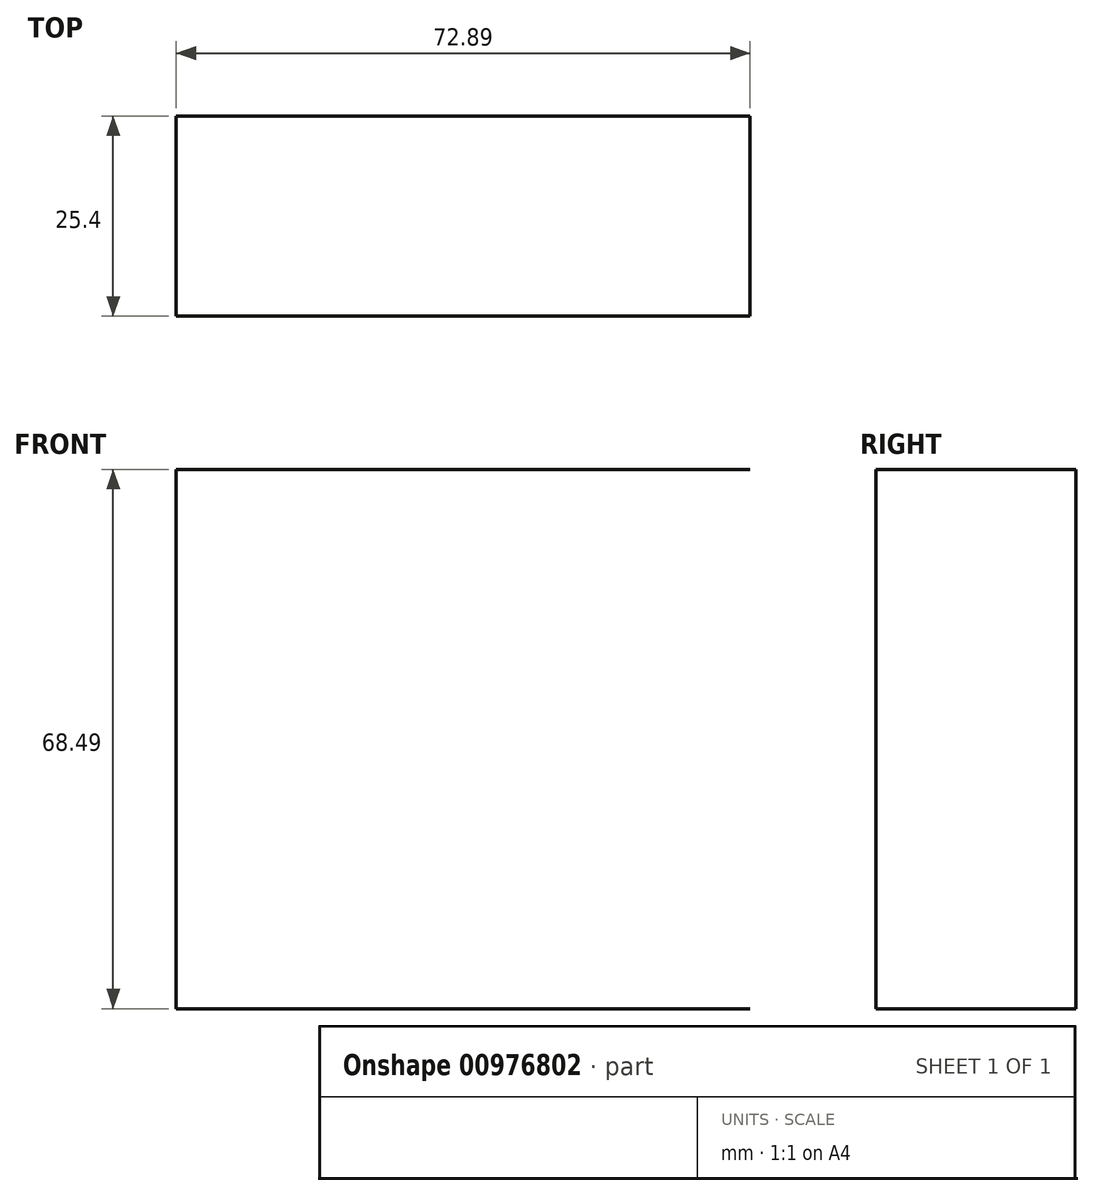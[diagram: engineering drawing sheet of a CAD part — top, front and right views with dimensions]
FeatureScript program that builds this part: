
annotation { "Feature Type Name" : "Feature", "Feature Type Description" : "" }
export const myFeature = defineFeature(function(context is Context, id is Id, definition is map)
    precondition{}
    {
        {
            var Q0;
            Q0=qCreatedBy(makeId("Front.planeOp"),FACE);
            var sketch = newSketch(context, id + "F0", { "sketchPlane" : qUnion([Q0])});
            skLineSegment(sketch, "E0.bottom", {"start": v(0, 0) * mm, "end": v(0, 0) * mm});
            skLineSegment(sketch, "E0.top", {"start": v(0, 0) * mm, "end": v(0, 0) * mm});
            skLineSegment(sketch, "E0.left", {"start": v(0, 0) * mm, "end": v(0, 0) * mm});
            skLineSegment(sketch, "E0.right", {"start": v(0, 0) * mm, "end": v(0, 0) * mm});
            skLineSegment(sketch, "E1.bottom", {"start": v(0, 0) * mm, "end": v(-72.89, 0) * mm});
            skLineSegment(sketch, "E1.top", {"start": v(0, -68.49) * mm, "end": v(-72.89, -68.49) * mm});
            skLineSegment(sketch, "E1.left", {"start": v(0, 0) * mm, "end": v(0, -68.49) * mm, "construction": true});
            skLineSegment(sketch, "E1.right", {"start": v(-72.89, 0) * mm, "end": v(-72.89, -68.49) * mm});
            skSolve(sketch);
        }
        {
            var Q0;
            Q0=sQuery(id+"F0.wireOp",EDGE,"E1.top");
            var Q1;
            Q1=sQuery(id+"F0.wireOp",EDGE,"E1.bottom");
            var Q2;
            Q2=sQuery(id+"F0.wireOp",EDGE,"E1.right");
            extrude(context, id + "F1", {"bodyType" : ToolBodyType.SURFACE, "surfaceEntities" : qUnion([Q0, Q1, Q2]), "depth" : 25.4 * mm, "offsetDistance" : 25.4 * mm});
        }
    });
